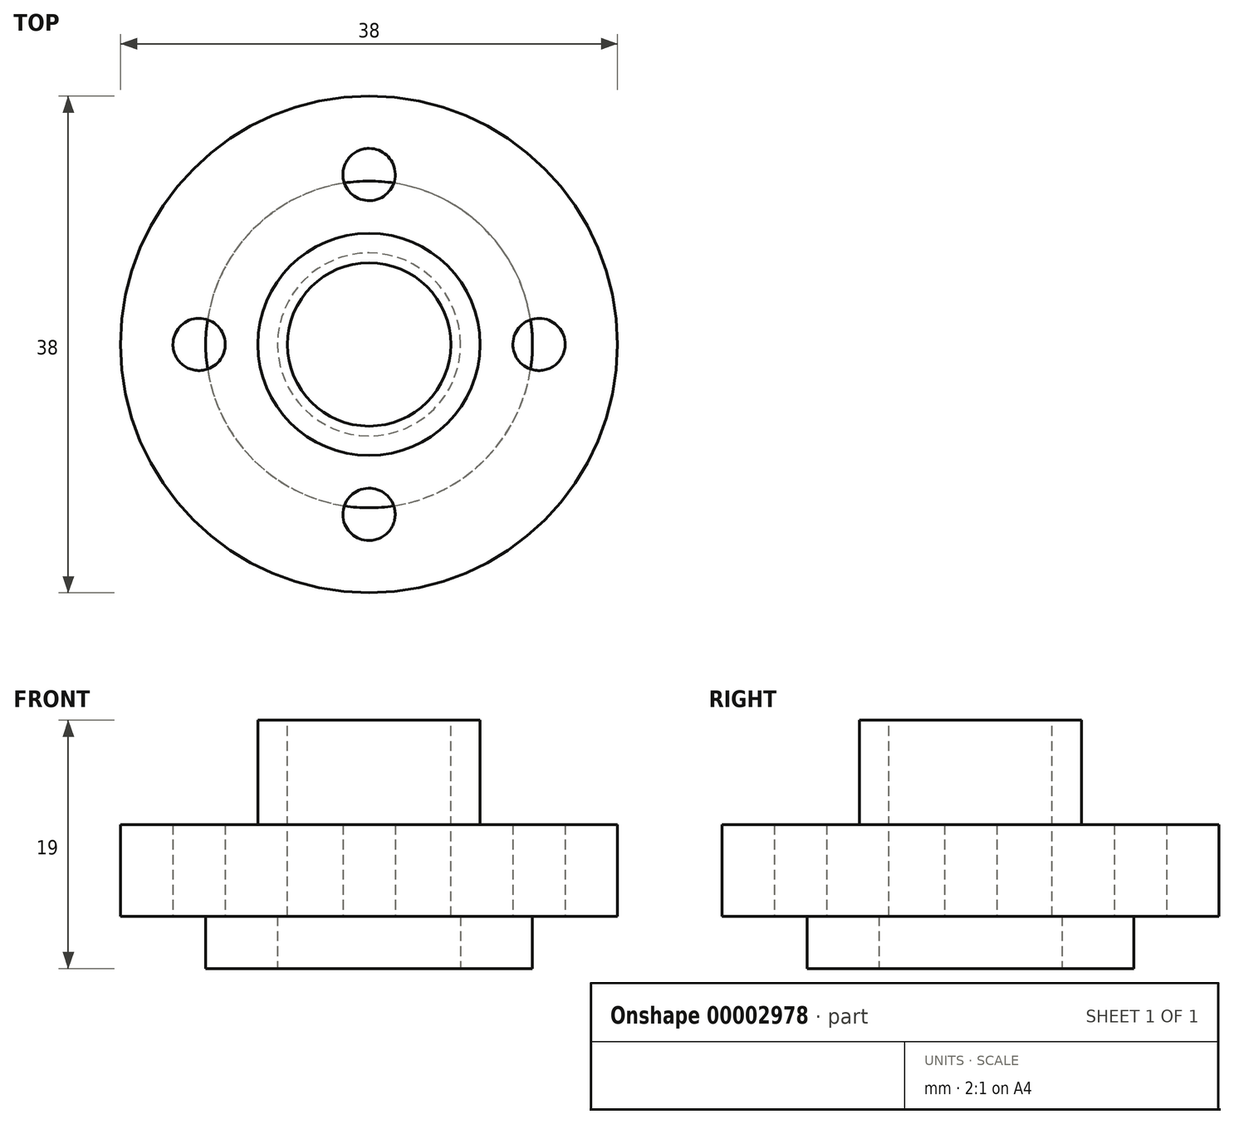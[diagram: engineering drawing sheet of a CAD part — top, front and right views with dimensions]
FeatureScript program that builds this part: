
annotation { "Feature Type Name" : "Feature", "Feature Type Description" : "" }
export const myFeature = defineFeature(function(context is Context, id is Id, definition is map)
    precondition{}
    {
        {
            var Q0;
            Q0=qCreatedBy(makeId("Top.planeOp"),FACE);
            var sketch = newSketch(context, id + "F0", { "sketchPlane" : qUnion([Q0])});
            skCircle(sketch, "E0", {"center": v(0, 0) * mm, "radius": 19 * mm});
            skSolve(sketch);
        }
        {
            var Q0;
            Q0 = qSketchRegion(id + "F0", true);
            extrude(context, id + "F1", {"entities" : qUnion([Q0]), "depth" : 7 * mm});
        }
        {
            var Q0;
            Q0 = qSketchRegion(id + "F0", true);
            var sketch = newSketch(context, id + "F2", { "sketchPlane" : qUnion([Q0])});
            skCircle(sketch, "E1", {"center": v(0, 0) * mm, "radius": 12.5 * mm});
            skSolve(sketch);
        }
        {
            var Q0;
            Q0=makeQuery(id+"F2.imprint","IMPRINT",FACE,{"disambiguationData":[TD([[makeQuery(id+"F2.imprint","IMPRINT",EDGE,{"derivedFrom":sQuery(id+"F2.wireOp",EDGE,"E1")}),1.0]])]});
            extrude(context, id + "F3", {"entities" : qUnion([Q0]), "operationType" : NewBodyOperationType.ADD, "oppositeDirection" : true, "depth" : 4 * mm});
        }
        {
            var Q0;
            Q0=makeQuery(id+"F1.opExtrude","CAP_FACE",FACE,{"disambiguationData":[OSD([sQuery(id+"F0.wireOp",EDGE,"E0")])],"isStart":false});
            var sketch = newSketch(context, id + "F4", { "sketchPlane" : qUnion([Q0])});
            skCircle(sketch, "E2", {"center": v(0, 0) * mm, "radius": 8.5 * mm});
            skSolve(sketch);
        }
        {
            var Q0;
            Q0=makeQuery(id+"F4.imprint","IMPRINT",FACE,{"disambiguationData":[TD([[makeQuery(id+"F4.imprint","IMPRINT",EDGE,{"derivedFrom":sQuery(id+"F4.wireOp",EDGE,"E2")}),1.0]])]});
            extrude(context, id + "F5", {"entities" : qUnion([Q0]), "operationType" : NewBodyOperationType.ADD, "depth" : 8 * mm});
        }
        {
            var Q0;
            Q0=makeQuery(id+"F0.imprint","IMPRINT",FACE,{"disambiguationData":[TD([[makeQuery(id+"F0.imprint","IMPRINT",EDGE,{"derivedFrom":sQuery(id+"F0.wireOp",EDGE,"E0")}),1.0]])]});
            var sketch = newSketch(context, id + "F6", { "sketchPlane" : qUnion([Q0])});
            skCircle(sketch, "E3", {"center": v(0, 0) * mm, "radius": 7 * mm});
            skSolve(sketch);
        }
        {
            var Q0;
            Q0=makeQuery(id+"F6.imprint","IMPRINT",FACE,{"disambiguationData":[TD([[makeQuery(id+"F6.imprint","IMPRINT",EDGE,{"derivedFrom":sQuery(id+"F6.wireOp",EDGE,"E3")}),1.0]])]});
            extrude(context, id + "F7", {"entities" : qUnion([Q0]), "operationType" : NewBodyOperationType.REMOVE, "endBound" : BoundingType.SYMMETRIC, "depth" : 8 * mm});
        }
        {
            var Q0;
            Q0=makeQuery(id+"F5.opExtrude","CAP_FACE",FACE,{"disambiguationData":[OSD([sQuery(id+"F4.wireOp",EDGE,"E2")])],"isStart":false});
            var sketch = newSketch(context, id + "F8", { "sketchPlane" : qUnion([Q0])});
            skCircle(sketch, "E4", {"center": v(0, 0) * mm, "radius": 6.25 * mm});
            skSolve(sketch);
        }
        {
            var Q0;
            Q0=makeQuery(id+"F8.imprint","IMPRINT",FACE,{"disambiguationData":[TD([[makeQuery(id+"F8.imprint","IMPRINT",EDGE,{"derivedFrom":sQuery(id+"F8.wireOp",EDGE,"E4")}),1.0]])]});
            extrude(context, id + "F9", {"entities" : qUnion([Q0]), "operationType" : NewBodyOperationType.REMOVE, "oppositeDirection" : true, "depth" : 50 * mm});
        }
        {
            var Q0;
            Q0=qCreatedBy(makeId("Front.planeOp"),FACE);
            var sketch = newSketch(context, id + "F10", { "sketchPlane" : qUnion([Q0])});
            skLineSegment(sketch, "E5", {"start": v(0, 0) * mm, "end": v(0, -38.01) * mm, "construction": true});
            skSolve(sketch);
        }
        {
            var Q0;
            Q0=makeQuery(id+"F1.opExtrude","CAP_FACE",FACE,{"disambiguationData":[OSD([sQuery(id+"F0.wireOp",EDGE,"E0")])],"isStart":true});
            var sketch = newSketch(context, id + "F11", { "sketchPlane" : qUnion([Q0])});
            skLineSegment(sketch, "E6", {"start": v(0, 0) * mm, "end": v(13, 0) * mm, "construction": true});
            skCircle(sketch, "E7", {"center": v(13, 0) * mm, "radius": 2 * mm});
            skSolve(sketch);
        }
        {
            var Q0;
            Q0 = qSketchRegion(id + "F11", true);
            extrude(context, id + "F12", {"entities" : qUnion([Q0]), "endBound" : BoundingType.UP_TO_NEXT, "oppositeDirection" : true, "depth" : 5 * mm});
        }
        {
            var Q0;
            Q0=makeQuery(id+"F12.opExtrude","SWEPT_BODY",BODY,{"disambiguationData":[OSD([sQuery(id+"F11.wireOp",EDGE,"E7")])]});
            var Q1;
            Q1=sQuery(id+"F10.wireOp",EDGE,"E5");
            circularPattern(context, id + "F13", {"operationType" : NewBodyOperationType.REMOVE, "entities" : qUnion([Q0]), "axis" : qUnion([Q1]), "angle" : 360 * degree, "instanceCount" : 4, "equalSpace" : true});
        }
        {
            var Q0;
            Q0=makeQuery(id+"F7.boolean.opBoolean","COPY",FACE,{"derivedFrom":makeQuery(id+"F7.opExtrude","CAP_FACE",FACE,{"disambiguationData":[OSD([sQuery(id+"F6.wireOp",EDGE,"E3")])],"isStart":false})});
            extrude(context, id + "F14", {"entities" : qUnion([Q0]), "operationType" : NewBodyOperationType.ADD, "depth" : 4 * mm});
        }
    });
